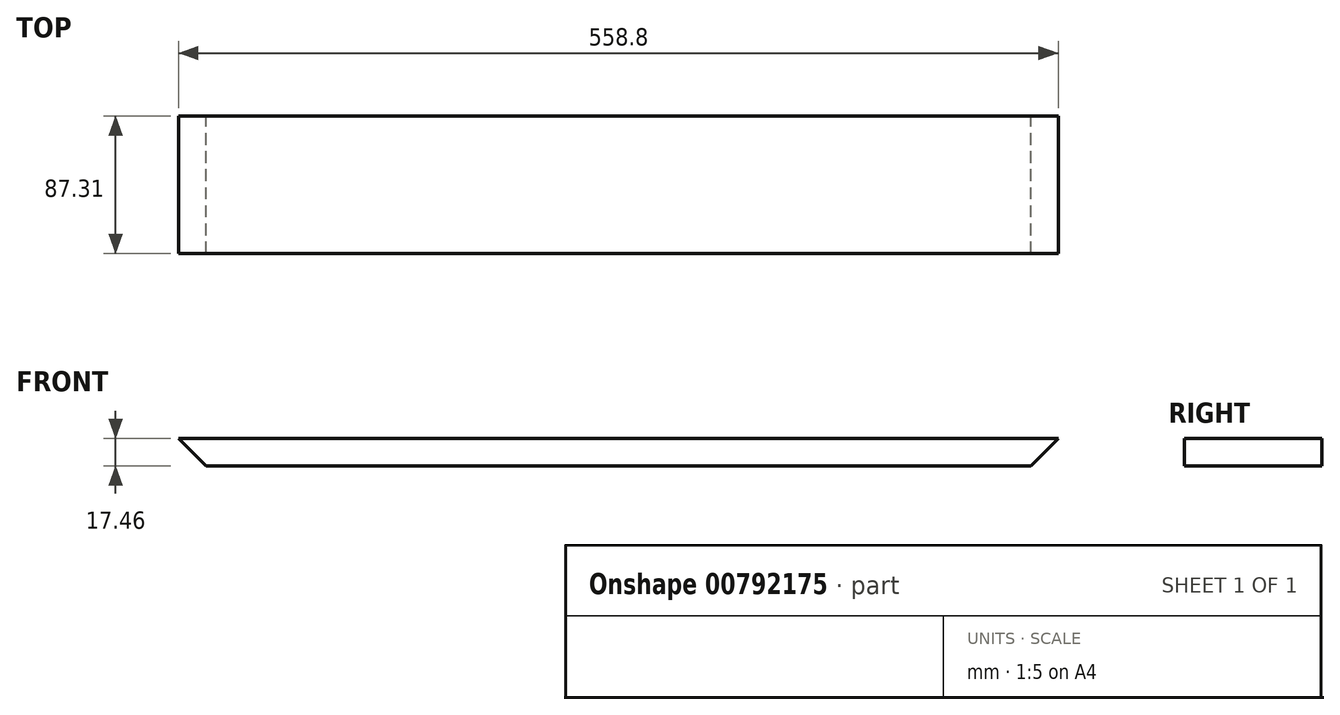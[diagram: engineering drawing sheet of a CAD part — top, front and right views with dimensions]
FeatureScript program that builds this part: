
annotation { "Feature Type Name" : "Feature", "Feature Type Description" : "" }
export const myFeature = defineFeature(function(context is Context, id is Id, definition is map)
    precondition{}
    {
        {
            var Q0;
            Q0=qCreatedBy(makeId("Top.planeOp"),FACE);
            var sketch = newSketch(context, id + "F0", { "sketchPlane" : qUnion([Q0])});
            skLineSegment(sketch, "E0.bottom", {"start": v(0, 0) * mm, "end": v(-558.8, 0) * mm});
            skLineSegment(sketch, "E0.top", {"start": v(0, 87.31) * mm, "end": v(-558.8, 87.31) * mm});
            skLineSegment(sketch, "E0.left", {"start": v(0, 0) * mm, "end": v(0, 87.31) * mm});
            skLineSegment(sketch, "E0.right", {"start": v(-558.8, 0) * mm, "end": v(-558.8, 87.31) * mm});
            skSolve(sketch);
        }
        {
            var Q0;
            Q0 = qSketchRegion(id + "F0", true);
            extrude(context, id + "F1", {"entities" : qUnion([Q0]), "depth" : 17.46 * mm, "offsetDistance" : 25.4 * mm});
        }
        {
            var Q0;
            Q0=makeQuery(id+"F1.opExtrude","SWEPT_FACE",FACE,{"disambiguationData":[OSD([sQuery(id+"F0.wireOp",EDGE,"E0.top")])]});
            var sketch = newSketch(context, id + "F2", { "sketchPlane" : qUnion([Q0])});
            skLineSegment(sketch, "E1", {"start": v(0, 17.46) * mm, "end": v(0, 0) * mm});
            skLineSegment(sketch, "E2", {"start": v(0, 0) * mm, "end": v(17.46, 0) * mm});
            skLineSegment(sketch, "E3", {"start": v(17.46, 0) * mm, "end": v(0, 17.46) * mm});
            skLineSegment(sketch, "E4", {"start": v(279.4, -11.18) * mm, "end": v(279.4, 37.86) * mm, "construction": true});
            skPoint(sketch, "E4.startSnap0", {"position": v(279.4, 0) * mm});
            skPoint(sketch, "E4.endSnap0", {"position": v(279.4, 17.46) * mm});
            skLineSegment(sketch, "E5.MirrorCS", {"start": v(558.8, 17.46) * mm, "end": v(558.8, 0) * mm});
            skLineSegment(sketch, "E6.MirrorCS", {"start": v(541.34, 0) * mm, "end": v(558.8, 17.46) * mm});
            skLineSegment(sketch, "E7.MirrorCS", {"start": v(558.8, 0) * mm, "end": v(541.34, 0) * mm});
            skSolve(sketch);
        }
        {
            var Q0;
            Q0 = qSketchRegion(id + "F2", true);
            extrude(context, id + "F3", {"entities" : qUnion([Q0]), "operationType" : NewBodyOperationType.REMOVE, "oppositeDirection" : true, "depth" : 87.31 * mm, "offsetDistance" : 25.4 * mm});
        }
    });
